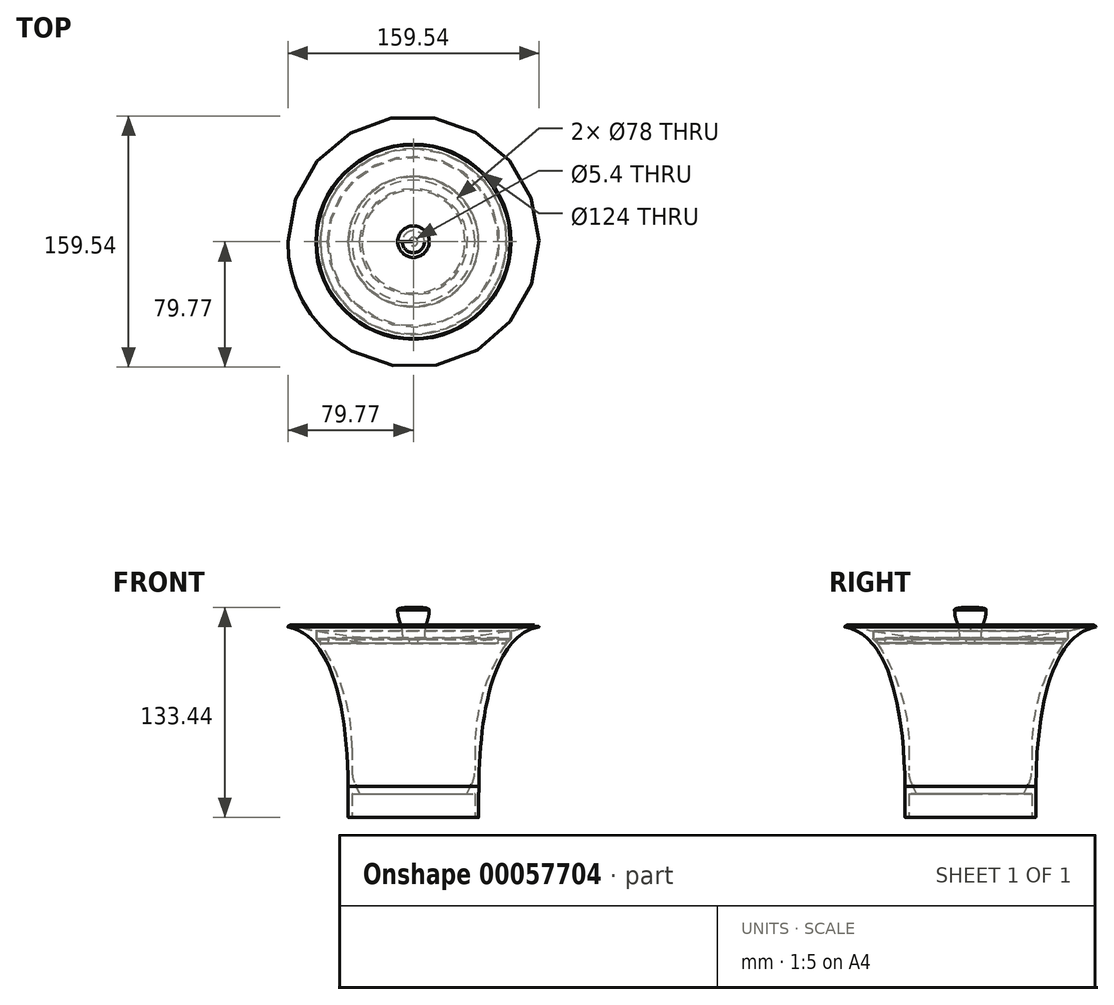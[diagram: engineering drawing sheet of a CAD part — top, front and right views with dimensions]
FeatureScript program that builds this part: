
annotation { "Feature Type Name" : "Feature", "Feature Type Description" : "" }
export const myFeature = defineFeature(function(context is Context, id is Id, definition is map)
    precondition{}
    {
        {
            var Q0;
            Q0=qCreatedBy(makeId("Front.planeOp"),FACE);
            var sketch = newSketch(context, id + "F0", { "sketchPlane" : qUnion([Q0])});
            skLineSegment(sketch, "E0", {"start": v(0, -15) * mm, "end": v(-39, -15) * mm, "construction": true});
            skLineSegment(sketch, "E1", {"start": v(0, 0) * mm, "end": v(0, -15) * mm, "construction": true});
            skLineSegment(sketch, "E2", {"start": v(-80, 103.5) * mm, "end": v(-62, 103.5) * mm, "construction": true});
            skLineSegment(sketch, "E3", {"start": v(-80, 106) * mm, "end": v(-30, 106) * mm, "construction": true});
            skLineSegment(sketch, "E4", {"start": v(-30, 106) * mm, "end": v(-30, 98) * mm, "construction": true});
            skLineSegment(sketch, "E5", {"start": v(-80, 106) * mm, "end": v(0, 106) * mm, "construction": true});
            skLineSegment(sketch, "E6", {"start": v(0, 0) * mm, "end": v(0, 106) * mm, "construction": true});
            skPoint(sketch, "E6.endSnap0", {"position": v(-55, 106) * mm});
            skLineSegment(sketch, "E7", {"start": v(-80, 106) * mm, "end": v(-80, 103.5) * mm, "construction": true});
            skLineSegment(sketch, "E8", {"start": v(-73.84, 105.47) * mm, "end": v(-62, 103.5) * mm, "construction": true});
            skLineSegment(sketch, "E9", {"start": v(-62, 103.5) * mm, "end": v(-58.05, 102.84) * mm, "construction": true});
            skPoint(sketch, "E10.visualSharp", {"position": v(-80, 106) * mm});
            skPoint(sketch, "E11.visualSharp", {"position": v(-62, 103.5) * mm});
            skLineSegment(sketch, "E12", {"start": v(-39, -14.8) * mm, "end": v(-39, -0.2) * mm});
            skLineSegment(sketch, "E13", {"start": v(-38.8, 0) * mm, "end": v(-34.32, 0) * mm});
            skLineSegment(sketch, "E14", {"start": v(-62, 98.5) * mm, "end": v(-59, 98.5) * mm, "construction": true});
            skLineSegment(sketch, "E15", {"start": v(-59, 98.5) * mm, "end": v(-59, 95.5) * mm, "construction": true});
            skLineSegment(sketch, "E16", {"start": v(-61.94, 98.44) * mm, "end": v(-59, 95.5) * mm});
            skLineSegment(sketch, "E17", {"start": v(-39.2, -15) * mm, "end": v(-41.3, -15) * mm});
            skLineSegment(sketch, "E18", {"start": v(-41.5, -14.8) * mm, "end": v(-41.5, 0) * mm});
            skLineSegment(sketch, "E19", {"start": v(-80, 106) * mm, "end": v(-80, 116) * mm, "construction": true});
            skLineSegment(sketch, "E20", {"start": v(-80, 116) * mm, "end": v(-70, 116) * mm, "construction": true});
            skLineSegment(sketch, "E21", {"start": v(-80, 106) * mm, "end": v(-70, 116) * mm, "construction": true});
            skLineSegment(sketch, "E22", {"start": v(-80, 106) * mm, "end": v(-76.46, 109.54) * mm, "construction": true});
            skLineSegment(sketch, "E23", {"start": v(-62, 103.5) * mm, "end": v(-62, 105.5) * mm, "construction": true});
            skLineSegment(sketch, "E24", {"start": v(-62, 105.5) * mm, "end": v(-74, 105.5) * mm, "construction": true});
            skLineSegment(sketch, "E25", {"start": v(-74, 105.5) * mm, "end": v(-62, 103.5) * mm, "construction": true});
            skLineSegment(sketch, "E26", {"start": v(-62, 103.33) * mm, "end": v(-62, 98.58) * mm});
            skFitSpline(sketch, "E27", {"points": [v(-80, 106) * mm, v(-62, 103.5) * mm], "startDerivative": vector(10.6, 10.6) * mm, "endDerivative": vector(35.51, -5.92) * mm});
            skFitSpline(sketch, "E28", {"points": [v(-80, 106) * mm, v(-41.5, 0) * mm], "startDerivative": vector(82.95, -13.27) * mm, "endDerivative": vector(0, -168) * mm});
            skLineSegment(sketch, "E29", {"start": v(-41.5, 0) * mm, "end": v(-41.5, 56) * mm, "construction": true});
            skLineSegment(sketch, "E30", {"start": v(-80, 106) * mm, "end": v(-52.35, 101.58) * mm, "construction": true});
            skLineSegment(sketch, "E31", {"start": v(-80, 106) * mm, "end": v(-30, 98) * mm, "construction": true});
            skLineSegment(sketch, "E32", {"start": v(-159, 29.17) * mm, "end": v(-59, 95.5) * mm, "construction": true});
            skLineSegment(sketch, "E33", {"start": v(-39, 14.72) * mm, "end": v(-39, 29.17) * mm});
            skArc(sketch, "E34", {"start": v(-39, 29.17) * mm, "mid": v(-44.1, 63.8) * mm, "end": v(-59, 95.5) * mm});
            skLineSegment(sketch, "E35", {"start": v(-55.2, 89.38) * mm, "end": v(-57.25, 88.2) * mm, "construction": true});
            skLineSegment(sketch, "E36", {"start": v(-159, 29.17) * mm, "end": v(-59, 29.17) * mm, "construction": true});
            skLineSegment(sketch, "E37", {"start": v(-59, 29.17) * mm, "end": v(-59, 95.5) * mm, "construction": true});
            skArc(sketch, "E38.trimOffspring", {"start": v(-41.53, 4.68) * mm, "mid": v(-41.51, 4.74) * mm, "end": v(-41.5, 4.8) * mm});
            skLineSegment(sketch, "E39", {"start": v(-34, 0) * mm, "end": v(-34, 10) * mm, "construction": true});
            skLineSegment(sketch, "E40", {"start": v(-34, 10) * mm, "end": v(-39, 10) * mm, "construction": true});
            skLineSegment(sketch, "E41", {"start": v(-36.89, 5.78) * mm, "end": v(-34.14, 0.29) * mm});
            skPoint(sketch, "E42.visualSharp", {"position": v(-39, 10) * mm});
            skArc(sketch, "E42.filletArc", {"start": v(-39, 14.72) * mm, "mid": v(-38.46, 10.13) * mm, "end": v(-36.89, 5.78) * mm});
            skPoint(sketch, "E43.visualSharp", {"position": v(-34, 0) * mm});
            skArc(sketch, "E43.filletArc", {"start": v(-34.32, 0) * mm, "mid": v(-34.15, 0.1) * mm, "end": v(-34.14, 0.29) * mm});
            skPoint(sketch, "E44.visualSharp", {"position": v(-39, -15) * mm});
            skArc(sketch, "E44.filletArc", {"start": v(-39.2, -15) * mm, "mid": v(-39.06, -14.94) * mm, "end": v(-39, -14.8) * mm});
            skPoint(sketch, "E45.visualSharp", {"position": v(-41.5, -15) * mm});
            skArc(sketch, "E45.filletArc", {"start": v(-41.5, -14.8) * mm, "mid": v(-41.44, -14.94) * mm, "end": v(-41.3, -15) * mm});
            skPoint(sketch, "E46.visualSharp", {"position": v(-39, 0) * mm});
            skArc(sketch, "E46.filletArc", {"start": v(-38.8, 0) * mm, "mid": v(-38.94, -0.06) * mm, "end": v(-39, -0.2) * mm});
            skArc(sketch, "E47.filletArc", {"start": v(-79.7, 106.28) * mm, "mid": v(-79.76, 106.08) * mm, "end": v(-79.6, 105.93) * mm});
            skArc(sketch, "E48.filletArc", {"start": v(-62, 103.33) * mm, "mid": v(-62.05, 103.46) * mm, "end": v(-62.17, 103.53) * mm});
            skPoint(sketch, "E49.visualSharp", {"position": v(-62, 98.5) * mm});
            skArc(sketch, "E49.filletArc", {"start": v(-62, 98.58) * mm, "mid": v(-61.98, 98.5) * mm, "end": v(-61.94, 98.44) * mm});
            skSolve(sketch);
        }
        {
            var Q0;
            Q0=makeQuery(id+"F0.imprint","IMPRINT",FACE,{"disambiguationData":[TD([[makeQuery(id+"F0.imprint","IMPRINT",EDGE,{"derivedFrom":sQuery(id+"F0.wireOp",EDGE,"E12")}),1.0]])]});
            var Q1;
            Q1=sQuery(id+"F0.wireOp",EDGE,"E6");
            revolve(context, id + "F1", {"surfaceOperationType" : NewSurfaceOperationType.NEW, "entities" : qUnion([Q0]), "axis" : qUnion([Q1]), "revolveType" : RevolveType.FULL});
        }
        {
            var Q0;
            Q0=qCreatedBy(makeId("Front.planeOp"),FACE);
            var sketch = newSketch(context, id + "F2", { "sketchPlane" : qUnion([Q0])});
            skLineSegment(sketch, "E50", {"start": v(-62, 103.42) * mm, "end": v(-61.5, 103.42) * mm, "construction": true});
            skLineSegment(sketch, "E51", {"start": v(-60.47, 96.97) * mm, "end": v(-60.12, 97.32) * mm, "construction": true});
            skLineSegment(sketch, "E52", {"start": v(-61.44, 98.65) * mm, "end": v(-60.9, 98.1) * mm});
            skLineSegment(sketch, "E53", {"start": v(-58.73, 95.94) * mm, "end": v(-58.73, 98.7) * mm, "construction": true});
            skLineSegment(sketch, "E54", {"start": v(-58.73, 98.7) * mm, "end": v(-61.5, 98.7) * mm, "construction": true});
            skLineSegment(sketch, "E55", {"start": v(-61.5, 103.18) * mm, "end": v(-61.5, 98.79) * mm});
            skLineSegment(sketch, "E56", {"start": v(-58.65, 95.94) * mm, "end": v(-54, 95.94) * mm});
            skLineSegment(sketch, "E57", {"start": v(-53.73, 95.94) * mm, "end": v(-53.73, 98.94) * mm, "construction": true});
            skLineSegment(sketch, "E58", {"start": v(-53.73, 98.94) * mm, "end": v(-54.53, 98.94) * mm, "construction": true});
            skLineSegment(sketch, "E59", {"start": v(-53.8, 96.2) * mm, "end": v(-54.46, 98.65) * mm});
            skLineSegment(sketch, "E60", {"start": v(0, 95.94) * mm, "end": v(-2.7, 95.94) * mm, "construction": true});
            skLineSegment(sketch, "E61", {"start": v(-2.7, 96.14) * mm, "end": v(-2.7, 98.24) * mm});
            skLineSegment(sketch, "E62", {"start": v(0, 98.44) * mm, "end": v(-10, 98.44) * mm, "construction": true});
            skLineSegment(sketch, "E63", {"start": v(-2.9, 98.44) * mm, "end": v(-10, 98.44) * mm});
            skLineSegment(sketch, "E64", {"start": v(-2.9, 95.94) * mm, "end": v(-32.7, 95.94) * mm});
            skLineSegment(sketch, "E65", {"start": v(-32.7, 95.94) * mm, "end": v(-54.24, 98.9) * mm});
            skLineSegment(sketch, "E66", {"start": v(-60.12, 97.32) * mm, "end": v(-59.12, 97.32) * mm, "construction": true});
            skArc(sketch, "E67", {"start": v(-59.35, 96.68) * mm, "mid": v(-59.41, 98.03) * mm, "end": v(-60.76, 98.1) * mm});
            skLineSegment(sketch, "E68.trimOffspring", {"start": v(-59.34, 96.55) * mm, "end": v(-58.8, 96) * mm});
            skFitSpline(sketch, "E69", {"points": [v(-61.5, 103.42) * mm, v(-10, 98.44) * mm], "startDerivative": vector(35.51, -5.92) * mm, "endDerivative": vector(66, 0) * mm});
            skLineSegment(sketch, "E70", {"start": v(-10, 98.44) * mm, "end": v(-32, 98.44) * mm, "construction": true});
            skPoint(sketch, "E71.endSnap0", {"position": v(-61.5, 101.06) * mm});
            skLineSegment(sketch, "E72", {"start": v(-61.27, 103.38) * mm, "end": v(-49.66, 101.44) * mm, "construction": true});
            skPoint(sketch, "E73.visualSharp", {"position": v(-53.73, 95.94) * mm});
            skArc(sketch, "E73.filletArc", {"start": v(-54, 95.94) * mm, "mid": v(-53.84, 96.02) * mm, "end": v(-53.8, 96.2) * mm});
            skPoint(sketch, "E74.visualSharp", {"position": v(-54.53, 98.94) * mm});
            skArc(sketch, "E74.filletArc", {"start": v(-54.24, 98.9) * mm, "mid": v(-54.41, 98.83) * mm, "end": v(-54.46, 98.65) * mm});
            skPoint(sketch, "E75.visualSharp", {"position": v(-58.73, 95.94) * mm});
            skArc(sketch, "E75.filletArc", {"start": v(-58.8, 96) * mm, "mid": v(-58.73, 95.96) * mm, "end": v(-58.65, 95.94) * mm});
            skPoint(sketch, "E76.visualSharp", {"position": v(-59.41, 96.62) * mm});
            skArc(sketch, "E76.filletArc", {"start": v(-59.35, 96.68) * mm, "mid": v(-59.37, 96.62) * mm, "end": v(-59.34, 96.55) * mm});
            skPoint(sketch, "E77.visualSharp", {"position": v(-60.82, 98.03) * mm});
            skArc(sketch, "E77.filletArc", {"start": v(-60.9, 98.1) * mm, "mid": v(-60.83, 98.07) * mm, "end": v(-60.76, 98.1) * mm});
            skPoint(sketch, "E78.visualSharp", {"position": v(-61.5, 98.7) * mm});
            skArc(sketch, "E78.filletArc", {"start": v(-61.5, 98.79) * mm, "mid": v(-61.48, 98.71) * mm, "end": v(-61.44, 98.65) * mm});
            skArc(sketch, "E79.filletArc", {"start": v(-61.27, 103.38) * mm, "mid": v(-61.43, 103.33) * mm, "end": v(-61.5, 103.18) * mm});
            skPoint(sketch, "E80.visualSharp", {"position": v(-2.7, 95.94) * mm});
            skArc(sketch, "E80.filletArc", {"start": v(-2.9, 95.94) * mm, "mid": v(-2.76, 96) * mm, "end": v(-2.7, 96.14) * mm});
            skPoint(sketch, "E81.visualSharp", {"position": v(-2.7, 98.44) * mm});
            skArc(sketch, "E81.filletArc", {"start": v(-2.7, 98.24) * mm, "mid": v(-2.76, 98.38) * mm, "end": v(-2.9, 98.44) * mm});
            skSolve(sketch);
        }
        {
            var Q0;
            Q0=makeQuery(id+"F2.imprint","IMPRINT",FACE,{"disambiguationData":[TD([[makeQuery(id+"F2.imprint","IMPRINT",EDGE,{"derivedFrom":sQuery(id+"F2.wireOp",EDGE,"E52")}),1.0]])]});
            var Q1;
            Q1=sQuery(id+"F0.wireOp",EDGE,"E6");
            revolve(context, id + "F3", {"surfaceOperationType" : NewSurfaceOperationType.NEW, "entities" : qUnion([Q0]), "axis" : qUnion([Q1]), "revolveType" : RevolveType.FULL});
        }
        {
            var Q0;
            Q0=qCreatedBy(makeId("Front.planeOp"),FACE);
            var sketch = newSketch(context, id + "F4", { "sketchPlane" : qUnion([Q0])});
            skLineSegment(sketch, "E82", {"start": v(0, 118.44) * mm, "end": v(-10, 118.44) * mm, "construction": true});
            skLineSegment(sketch, "E83", {"start": v(-10, 118.44) * mm, "end": v(-10, 116.94) * mm, "construction": true});
            skFitSpline(sketch, "E84", {"points": [v(0, 118.44) * mm, v(-10, 116.94) * mm], "startDerivative": vector(-18, 0) * mm, "endDerivative": vector(0, -3) * mm});
            skFitSpline(sketch, "E85", {"points": [v(-10, 116.94) * mm, v(-7, 98.44) * mm], "startDerivative": vector(0, -24) * mm, "endDerivative": vector(0, -33) * mm});
            skLineSegment(sketch, "E86", {"start": v(-7, 98.44) * mm, "end": v(-7, 109.44) * mm, "construction": true});
            skLineSegment(sketch, "E87", {"start": v(-10, 116.94) * mm, "end": v(-10, 117.94) * mm, "construction": true});
            skLineSegment(sketch, "E88", {"start": v(-10, 116.94) * mm, "end": v(-10, 108.94) * mm, "construction": true});
            skLineSegment(sketch, "E89", {"start": v(0, 118.44) * mm, "end": v(-6, 118.44) * mm, "construction": true});
            skLineSegment(sketch, "E90", {"start": v(-7, 98.44) * mm, "end": v(0, 98.44) * mm});
            skLineSegment(sketch, "E91", {"start": v(0, 118.44) * mm, "end": v(0, 98.44) * mm});
            skSolve(sketch);
        }
        {
            var Q0;
            Q0=makeQuery(id+"F4.imprint","IMPRINT",FACE,{"disambiguationData":[TD([[makeQuery(id+"F4.imprint","IMPRINT",EDGE,{"derivedFrom":sQuery(id+"F4.wireOp",EDGE,"E84")}),1.0]])]});
            var Q1;
            Q1=sQuery(id+"F4.wireOp",EDGE,"E91");
            revolve(context, id + "F5", {"surfaceOperationType" : NewSurfaceOperationType.NEW, "entities" : qUnion([Q0]), "axis" : qUnion([Q1]), "revolveType" : RevolveType.FULL});
        }
    });
